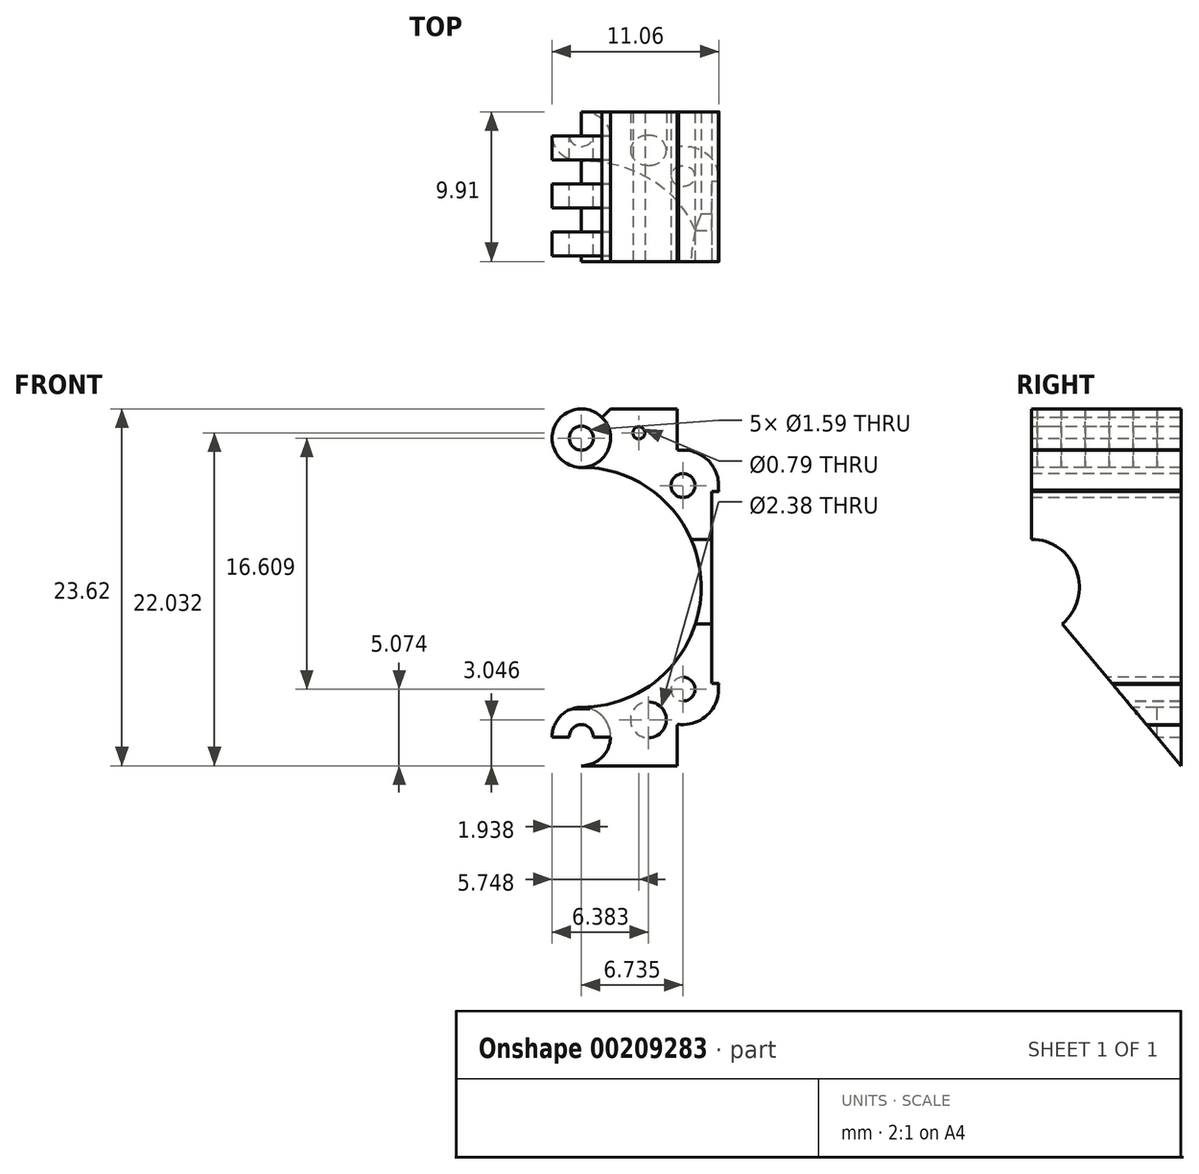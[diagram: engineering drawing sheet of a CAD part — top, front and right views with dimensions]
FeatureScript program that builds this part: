
annotation { "Feature Type Name" : "Feature", "Feature Type Description" : "" }
export const myFeature = defineFeature(function(context is Context, id is Id, definition is map)
    precondition{}
    {
        {
            var Q0;
            Q0=qCreatedBy(makeId("Front.planeOp"),FACE);
            var sketch = newSketch(context, id + "F0", { "sketchPlane" : qUnion([Q0])});
            skCircle(sketch, "E0", {"center": v(-2.61, -9.81) * mm, "radius": 7.94 * mm});
            skArc(sketch, "E1", {"start": v(6.45, -16.24) * mm, "mid": v(6.48, -16.2) * mm, "end": v(6.5, -16.16) * mm});
            skLineSegment(sketch, "E2", {"start": v(-2.61, 6.3) * mm, "end": v(-2.61, -28.6) * mm, "construction": true});
            skLineSegment(sketch, "E3", {"start": v(-21.52, -9.81) * mm, "end": v(15.73, -9.81) * mm, "construction": true});
            skLineSegment(sketch, "E4.bottom", {"start": v(-8.96, 2) * mm, "end": v(-4.55, 2) * mm});
            skLineSegment(sketch, "E4.top", {"start": v(-8.96, -1.18) * mm, "end": v(3.74, -1.18) * mm});
            skLineSegment(sketch, "E4.left", {"start": v(-8.96, 2) * mm, "end": v(-8.96, -1.18) * mm});
            skLineSegment(sketch, "E4.right", {"start": v(3.74, 2) * mm, "end": v(3.74, -1.18) * mm});
            skLineSegment(sketch, "E5.bottom", {"start": v(-8.96, -18.45) * mm, "end": v(3.74, -18.45) * mm});
            skLineSegment(sketch, "E5.top", {"start": v(-8.96, -21.62) * mm, "end": v(3.74, -21.62) * mm});
            skLineSegment(sketch, "E5.left", {"start": v(-8.96, -18.45) * mm, "end": v(-8.96, -21.62) * mm});
            skLineSegment(sketch, "E5.right", {"start": v(3.74, -18.45) * mm, "end": v(3.74, -21.62) * mm});
            skLineSegment(sketch, "E6.top", {"start": v(-11.73, -16.16) * mm, "end": v(-11.25, -16.16) * mm});
            skLineSegment(sketch, "E6.right", {"start": v(-11.25, -3.46) * mm, "end": v(-11.25, -16.16) * mm});
            skPoint(sketch, "E7.firstSnap0", {"position": v(-12.84, -3.46) * mm});
            skLineSegment(sketch, "E7.bottom", {"start": v(6.02, -3.46) * mm, "end": v(6.5, -3.46) * mm});
            skLineSegment(sketch, "E7.top", {"start": v(6.02, -16.16) * mm, "end": v(6.5, -16.16) * mm});
            skLineSegment(sketch, "E7.left", {"start": v(6.02, -3.46) * mm, "end": v(6.02, -16.16) * mm});
            skLineSegment(sketch, "E8", {"start": v(-2.61, -9.81) * mm, "end": v(9.55, -21.98) * mm, "construction": true});
            skLineSegment(sketch, "E9", {"start": v(-2.61, -9.81) * mm, "end": v(-14.5, -21.7) * mm, "construction": true});
            skLineSegment(sketch, "E10", {"start": v(-2.61, -9.81) * mm, "end": v(-14.78, 2.36) * mm, "construction": true});
            skLineSegment(sketch, "E11", {"start": v(-2.61, -9.81) * mm, "end": v(6.79, -0.41) * mm, "construction": true});
            skCircle(sketch, "E12", {"center": v(-2.61, -9.81) * mm, "radius": 9.53 * mm, "construction": true});
            skCircle(sketch, "E13", {"center": v(-9.35, -3.08) * mm, "radius": 0.8 * mm});
            skCircle(sketch, "E14", {"center": v(4.12, -3.08) * mm, "radius": 0.8 * mm});
            skCircle(sketch, "E15", {"center": v(-9.35, -16.55) * mm, "radius": 0.8 * mm});
            skCircle(sketch, "E16", {"center": v(4.12, -16.55) * mm, "radius": 0.8 * mm});
            skArc(sketch, "E17", {"start": v(-11.68, -16.24) * mm, "mid": v(-11, -18.2) * mm, "end": v(-9.04, -18.88) * mm});
            skArc(sketch, "E18", {"start": v(3.82, -18.88) * mm, "mid": v(5.78, -18.2) * mm, "end": v(6.45, -16.24) * mm});
            skArc(sketch, "E19.trimOffspring", {"start": v(-9.04, -0.75) * mm, "mid": v(-11, -1.41) * mm, "end": v(-11.68, -3.38) * mm});
            skArc(sketch, "E20.trimOffspring", {"start": v(-9.04, -18.88) * mm, "mid": v(-2.61, -20.92) * mm, "end": v(3.82, -18.88) * mm});
            skArc(sketch, "E21.trimOffspring", {"start": v(-11.68, -3.38) * mm, "mid": v(-11.7, -3.42) * mm, "end": v(-11.73, -3.46) * mm});
            skArc(sketch, "E22.trimOffspring", {"start": v(3.82, -0.75) * mm, "mid": v(-2.61, 1.3) * mm, "end": v(-9.04, -0.75) * mm});
            skArc(sketch, "E23.trimOffspring", {"start": v(6.45, -3.38) * mm, "mid": v(5.78, -1.41) * mm, "end": v(3.82, -0.75) * mm});
            skLineSegment(sketch, "E24", {"start": v(-2.61, -17.75) * mm, "end": v(3.74, -21.62) * mm, "construction": true});
            skPoint(sketch, "E25.startSnap0", {"position": v(0.56, -19.69) * mm});
            skCircle(sketch, "E26", {"center": v(-2.61, -19.69) * mm, "radius": 1.94 * mm});
            skLineSegment(sketch, "E27", {"start": v(1.2, 3.12) * mm, "end": v(1.2, -9.81) * mm, "construction": true});
            skLineSegment(sketch, "E28", {"start": v(-2.61, -1.87) * mm, "end": v(-8.96, 2) * mm, "construction": true});
            skLineSegment(sketch, "E29", {"start": v(-9.67, 0.06) * mm, "end": v(4.54, 0.06) * mm, "construction": true});
            skPoint(sketch, "E29.startSnap0", {"position": v(-5.79, 0.06) * mm});
            skCircle(sketch, "E30", {"center": v(-2.61, 0.06) * mm, "radius": 1.94 * mm});
            skLineSegment(sketch, "E31", {"start": v(-9.8, 0.41) * mm, "end": v(4.47, 0.41) * mm, "construction": true});
            skPoint(sketch, "E31.startSnap0", {"position": v(-8.96, 0.41) * mm});
            skPoint(sketch, "E31.endSnap0", {"position": v(3.74, 0.41) * mm});
            skCircle(sketch, "E32", {"center": v(-6.42, 0.41) * mm, "radius": 0.4 * mm});
            skCircle(sketch, "E33", {"center": v(1.2, 0.41) * mm, "radius": 0.4 * mm});
            skLineSegment(sketch, "E34.trimOffspring", {"start": v(-6.42, -9.81) * mm, "end": v(-6.42, 2.97) * mm, "construction": true});
            skLineSegment(sketch, "E35.trimOffspring", {"start": v(-0.68, -19.69) * mm, "end": v(-4.55, -19.69) * mm, "construction": true});
            skPoint(sketch, "E25.start.orphan", {"position": v(4.39, -19.69) * mm});
            skLineSegment(sketch, "E36", {"start": v(-7.06, -15.85) * mm, "end": v(-7.06, -22.98) * mm, "construction": true});
            skLineSegment(sketch, "E37", {"start": v(1.83, -22.98) * mm, "end": v(1.83, -15.78) * mm, "construction": true});
            skLineSegment(sketch, "E38", {"start": v(-7.95, -18.57) * mm, "end": v(-6.2, -18.57) * mm, "construction": true});
            skLineSegment(sketch, "E39", {"start": v(0.99, -18.57) * mm, "end": v(2.74, -18.57) * mm, "construction": true});
            skPoint(sketch, "E39.startSnap0", {"position": v(-7.08, -18.57) * mm});
            skCircle(sketch, "E40", {"center": v(-7.08, -18.57) * mm, "radius": 1.2 * mm});
            skCircle(sketch, "E41", {"center": v(1.83, -18.57) * mm, "radius": 1.2 * mm});
            skLineSegment(sketch, "E42.trimOffspring", {"start": v(-11.73, -3.46) * mm, "end": v(-11.25, -3.46) * mm});
            skArc(sketch, "E43.trimOffspring", {"start": v(-11.73, -16.16) * mm, "mid": v(-11.7, -16.2) * mm, "end": v(-11.68, -16.24) * mm});
            skPoint(sketch, "E6.left.start.orphan", {"position": v(-14.42, -3.46) * mm});
            skPoint(sketch, "E44.orphan", {"position": v(9.2, -16.16) * mm});
            skArc(sketch, "E45.trimOffspring", {"start": v(6.5, -3.46) * mm, "mid": v(6.48, -3.42) * mm, "end": v(6.45, -3.38) * mm});
            skCircle(sketch, "E46", {"center": v(-2.61, 0.06) * mm, "radius": 0.97 * mm});
            skLineSegment(sketch, "E47", {"start": v(-2.61, 0.06) * mm, "end": v(-4.55, 2) * mm});
            skLineSegment(sketch, "E48", {"start": v(-0.68, 2) * mm, "end": v(-2.61, 0.06) * mm});
            skLineSegment(sketch, "E49.trimOffspring", {"start": v(-0.68, 2) * mm, "end": v(3.74, 2) * mm});
            skCircle(sketch, "E50", {"center": v(-2.61, -19.69) * mm, "radius": 0.98 * mm});
            skSolve(sketch);
        }
        {
            var Q0;
            {var subQ5=sQuery(id+"F0.wireOp",EDGE,"E49.trimOffspring");Q0=makeQuery(id+"F0.imprint","IMPRINT",FACE,{"disambiguationData":[TD([[makeQuery(id+"F0.imprint","IMPRINT",EDGE,{"derivedFrom":subQ5}),-1.0]])]});}
            var Q1;
            {var subQ6=sQuery(id+"F0.wireOp",EDGE,"E4.right");var subQ8=sQuery(id+"F0.wireOp",EDGE,"E4.top");var subQ9=makeQuery(id+"F0.imprint","INTERSECT",VERTEX,{"derivedFrom":[subQ8,subQ6]});Q1=makeQuery(id+"F0.imprint","IMPRINT",FACE,{"disambiguationData":[TD([[makeQuery(id+"F0.imprint","IMPRINT",EDGE,{"disambiguationData":[TD([[subQ9,1.0]])],"derivedFrom":subQ8}),1.0]])]});}
            var Q2;
            Q2=makeQuery(id+"F0.imprint","IMPRINT",FACE,{"disambiguationData":[TD([[makeQuery(id+"F0.imprint","IMPRINT",EDGE,{"derivedFrom":sQuery(id+"F0.wireOp",EDGE,"E1")}),1.0]])]});
            var Q3;
            {var subQ1=sQuery(id+"F0.wireOp",EDGE,"E5.bottom");var subQ5=sQuery(id+"F0.wireOp",EDGE,"E26");var subQ9=makeQuery(id+"F0.imprint","INTERSECT",VERTEX,{"disambiguationData":[OD(1.0)],"derivedFrom":[subQ1,subQ5]});Q3=makeQuery(id+"F0.imprint","IMPRINT",FACE,{"disambiguationData":[TD([[makeQuery(id+"F0.imprint","IMPRINT",EDGE,{"disambiguationData":[TD([[subQ9,-1.0]])],"derivedFrom":subQ1}),-1.0]])]});}
            var Q4;
            {var subQ0=sQuery(id+"F0.wireOp",EDGE,"E5.right");var subQ1=sQuery(id+"F0.wireOp",EDGE,"E5.top");var subQ2=makeQuery(id+"F0.imprint","INTERSECT",VERTEX,{"derivedFrom":[subQ1,subQ0]});Q4=makeQuery(id+"F0.imprint","IMPRINT",FACE,{"disambiguationData":[TD([[makeQuery(id+"F0.imprint","IMPRINT",EDGE,{"disambiguationData":[TD([[subQ2,1.0]])],"derivedFrom":subQ1}),1.0]])]});}
            extrude(context, id + "F1", {"entities" : qUnion([Q0, Q1, Q2, Q3, Q4]), "oppositeDirection" : true, "depth" : 25.4 * mm});
        }
        {
            var Q0;
            Q0=makeQuery(id+"F1.opExtrude","CAP_FACE",FACE,{"disambiguationData":[OSD([sQuery(id+"F0.wireOp",EDGE,"E0"),sQuery(id+"F0.wireOp",EDGE,"E1"),sQuery(id+"F0.wireOp",EDGE,"E4.right"),sQuery(id+"F0.wireOp",EDGE,"E5.top"),sQuery(id+"F0.wireOp",EDGE,"E5.right"),sQuery(id+"F0.wireOp",EDGE,"E7.bottom"),sQuery(id+"F0.wireOp",EDGE,"E7.top"),sQuery(id+"F0.wireOp",EDGE,"E7.left"),sQuery(id+"F0.wireOp",EDGE,"E14"),sQuery(id+"F0.wireOp",EDGE,"E16"),sQuery(id+"F0.wireOp",EDGE,"E18"),sQuery(id+"F0.wireOp",EDGE,"E20.trimOffspring"),sQuery(id+"F0.wireOp",EDGE,"E22.trimOffspring"),sQuery(id+"F0.wireOp",EDGE,"E23.trimOffspring"),sQuery(id+"F0.wireOp",EDGE,"E26"),sQuery(id+"F0.wireOp",EDGE,"E30"),sQuery(id+"F0.wireOp",EDGE,"E33"),sQuery(id+"F0.wireOp",EDGE,"E41"),sQuery(id+"F0.wireOp",EDGE,"E45.trimOffspring"),sQuery(id+"F0.wireOp",EDGE,"E48"),sQuery(id+"F0.wireOp",EDGE,"E49.trimOffspring")])],"isStart":false});
            var sketch = newSketch(context, id + "F2", { "sketchPlane" : qUnion([Q0])});
            skCircle(sketch, "E51", {"center": v(2.61, 0.06) * mm, "radius": 1.94 * mm});
            skCircle(sketch, "E52", {"center": v(2.61, -19.69) * mm, "radius": 1.94 * mm});
            skSolve(sketch);
        }
        {
            var Q0;
            Q0 = qSketchRegion(id + "F2", true);
            extrude(context, id + "F3", {"entities" : qUnion([Q0]), "operationType" : NewBodyOperationType.ADD, "oppositeDirection" : true, "depth" : 3.17 * mm, "hasSecondDirection" : true, "secondDirectionOppositeDirection" : true, "secondDirectionDepth" : 1.59 * mm});
        }
        {
            var Q0;
            Q0=makeQuery(id+"F3.opExtrude","CAP_FACE",FACE,{"disambiguationData":[OSD([sQuery(id+"F2.wireOp",EDGE,"E51")])],"isStart":false});
            var sketch = newSketch(context, id + "F4", { "sketchPlane" : qUnion([Q0])});
            skCircle(sketch, "E53", {"center": v(-2.61, 0.06) * mm, "radius": 1.94 * mm});
            skSolve(sketch);
        }
        {
            var Q0;
            Q0 = qSketchRegion(id + "F4", true);
            extrude(context, id + "F5", {"entities" : qUnion([Q0]), "operationType" : NewBodyOperationType.ADD, "depth" : 3.17 * mm, "hasSecondDirection" : true, "secondDirectionOppositeDirection" : false, "secondDirectionDepth" : 1.59 * mm});
        }
        {
            var Q0;
            Q0=makeQuery(id+"F5.opExtrude","CAP_FACE",FACE,{"disambiguationData":[OSD([sQuery(id+"F4.wireOp",EDGE,"E53")])],"isStart":false});
            var sketch = newSketch(context, id + "F6", { "sketchPlane" : qUnion([Q0])});
            skCircle(sketch, "E54", {"center": v(-2.61, 0.06) * mm, "radius": 1.94 * mm});
            skSolve(sketch);
        }
        {
            var Q0;
            Q0 = qSketchRegion(id + "F6", true);
            extrude(context, id + "F7", {"entities" : qUnion([Q0]), "operationType" : NewBodyOperationType.ADD, "depth" : 3.17 * mm, "hasSecondDirection" : true, "secondDirectionOppositeDirection" : false, "secondDirectionDepth" : 1.59 * mm});
        }
        {
            var Q0;
            Q0=makeQuery(id+"F7.opExtrude","CAP_FACE",FACE,{"disambiguationData":[OSD([sQuery(id+"F6.wireOp",EDGE,"E54")])],"isStart":false});
            var sketch = newSketch(context, id + "F8", { "sketchPlane" : qUnion([Q0])});
            skCircle(sketch, "E55", {"center": v(-2.61, 0.06) * mm, "radius": 1.94 * mm});
            skSolve(sketch);
        }
        {
            var Q0;
            Q0 = qSketchRegion(id + "F8", true);
            extrude(context, id + "F9", {"entities" : qUnion([Q0]), "operationType" : NewBodyOperationType.ADD, "depth" : 3.17 * mm, "hasSecondDirection" : true, "secondDirectionOppositeDirection" : false, "secondDirectionDepth" : 1.59 * mm});
        }
        {
            var Q0;
            Q0=makeQuery(id+"F9.opExtrude","CAP_FACE",FACE,{"disambiguationData":[OSD([sQuery(id+"F8.wireOp",EDGE,"E55")])],"isStart":false});
            var sketch = newSketch(context, id + "F10", { "sketchPlane" : qUnion([Q0])});
            skCircle(sketch, "E56", {"center": v(-2.61, 0.06) * mm, "radius": 1.94 * mm});
            skSolve(sketch);
        }
        {
            var Q0;
            Q0 = qSketchRegion(id + "F10", true);
            extrude(context, id + "F11", {"entities" : qUnion([Q0]), "operationType" : NewBodyOperationType.ADD, "depth" : 3.17 * mm, "hasSecondDirection" : true, "secondDirectionOppositeDirection" : false, "secondDirectionDepth" : 1.59 * mm});
        }
        {
            var Q0;
            Q0=makeQuery(id+"F3.opExtrude","CAP_FACE",FACE,{"disambiguationData":[OSD([sQuery(id+"F2.wireOp",EDGE,"E52")])],"isStart":false});
            var sketch = newSketch(context, id + "F12", { "sketchPlane" : qUnion([Q0])});
            skCircle(sketch, "E57", {"center": v(-2.61, -19.69) * mm, "radius": 1.94 * mm});
            skSolve(sketch);
        }
        {
            var Q0;
            Q0 = qSketchRegion(id + "F12", true);
            extrude(context, id + "F13", {"entities" : qUnion([Q0]), "operationType" : NewBodyOperationType.ADD, "depth" : 3.17 * mm, "hasSecondDirection" : true, "secondDirectionOppositeDirection" : false, "secondDirectionDepth" : 1.59 * mm});
        }
        {
            var Q0;
            Q0=makeQuery(id+"F3.opExtrude","CAP_FACE",FACE,{"disambiguationData":[OSD([sQuery(id+"F2.wireOp",EDGE,"E51")])],"isStart":true});
            var sketch = newSketch(context, id + "F14", { "sketchPlane" : qUnion([Q0])});
            skCircle(sketch, "E58", {"center": v(2.61, 0.06) * mm, "radius": 0.8 * mm});
            skSolve(sketch);
        }
        {
            var Q0;
            Q0 = qSketchRegion(id + "F14", true);
            extrude(context, id + "F15", {"entities" : qUnion([Q0]), "operationType" : NewBodyOperationType.REMOVE, "endBound" : BoundingType.THROUGH_ALL, "oppositeDirection" : true, "depth" : 25.4 * mm});
        }
        {
            var Q0;
            Q0=makeQuery(id+"F3.opExtrude","CAP_FACE",FACE,{"disambiguationData":[OSD([sQuery(id+"F2.wireOp",EDGE,"E52")])],"isStart":true});
            var sketch = newSketch(context, id + "F16", { "sketchPlane" : qUnion([Q0])});
            skCircle(sketch, "E59", {"center": v(2.61, -19.69) * mm, "radius": 0.8 * mm});
            skSolve(sketch);
        }
        {
            var Q0;
            Q0 = qSketchRegion(id + "F16", true);
            extrude(context, id + "F17", {"entities" : qUnion([Q0]), "operationType" : NewBodyOperationType.REMOVE, "endBound" : BoundingType.THROUGH_ALL, "oppositeDirection" : true, "depth" : 25.4 * mm});
        }
        {
            var Q0;
            Q0=makeQuery(id+"F1.opExtrude","SWEPT_FACE",FACE,{"disambiguationData":[OSD([sQuery(id+"F0.wireOp",EDGE,"E7.left")])]});
            var sketch = newSketch(context, id + "F18", { "sketchPlane" : qUnion([Q0])});
            skLineSegment(sketch, "E60", {"start": v(25.4, 5.92) * mm, "end": v(25.4, -27.33) * mm, "construction": true});
            skLineSegment(sketch, "E61", {"start": v(-2.25, -9.81) * mm, "end": v(27.57, -9.81) * mm, "construction": true});
            skPoint(sketch, "E61.startSnap0", {"position": v(0, -9.81) * mm});
            skLineSegment(sketch, "E62", {"start": v(19.9, -21.62) * mm, "end": v(29.8, -21.62) * mm, "construction": true});
            skLineSegment(sketch, "E63", {"start": v(25.4, -21.62) * mm, "end": v(15.49, -9.81) * mm});
            skLineSegment(sketch, "E64", {"start": v(15.49, -9.81) * mm, "end": v(15.49, 6.84) * mm});
            skLineSegment(sketch, "E65", {"start": v(15.49, 6.84) * mm, "end": v(-6.1, 6.84) * mm});
            skLineSegment(sketch, "E66", {"start": v(-6.1, 6.84) * mm, "end": v(-6.1, -25.8) * mm});
            skLineSegment(sketch, "E67", {"start": v(-6.1, -25.8) * mm, "end": v(21.93, -25.8) * mm});
            skLineSegment(sketch, "E68", {"start": v(21.93, -25.8) * mm, "end": v(25.4, -21.62) * mm});
            skSolve(sketch);
        }
        {
            var Q0;
            Q0 = qSketchRegion(id + "F18", true);
            extrude(context, id + "F19", {"entities" : qUnion([Q0]), "operationType" : NewBodyOperationType.REMOVE, "oppositeDirection" : true, "depth" : 25.4 * mm, "hasSecondDirection" : true, "secondDirectionOppositeDirection" : false, "secondDirectionDepth" : 25.4 * mm});
        }
        {
            var Q0;
            Q0=makeQuery(id+"F1.opExtrude","SWEPT_FACE",FACE,{"disambiguationData":[OSD([sQuery(id+"F0.wireOp",EDGE,"E7.left")])]});
            var sketch = newSketch(context, id + "F20", { "sketchPlane" : qUnion([Q0])});
            skCircle(sketch, "E69", {"center": v(15.49, -9.81) * mm, "radius": 3.18 * mm});
            skSolve(sketch);
        }
        {
            var Q0;
            Q0 = qSketchRegion(id + "F20", true);
            extrude(context, id + "F21", {"entities" : qUnion([Q0]), "operationType" : NewBodyOperationType.REMOVE, "oppositeDirection" : true, "depth" : 25.4 * mm});
        }
    });
